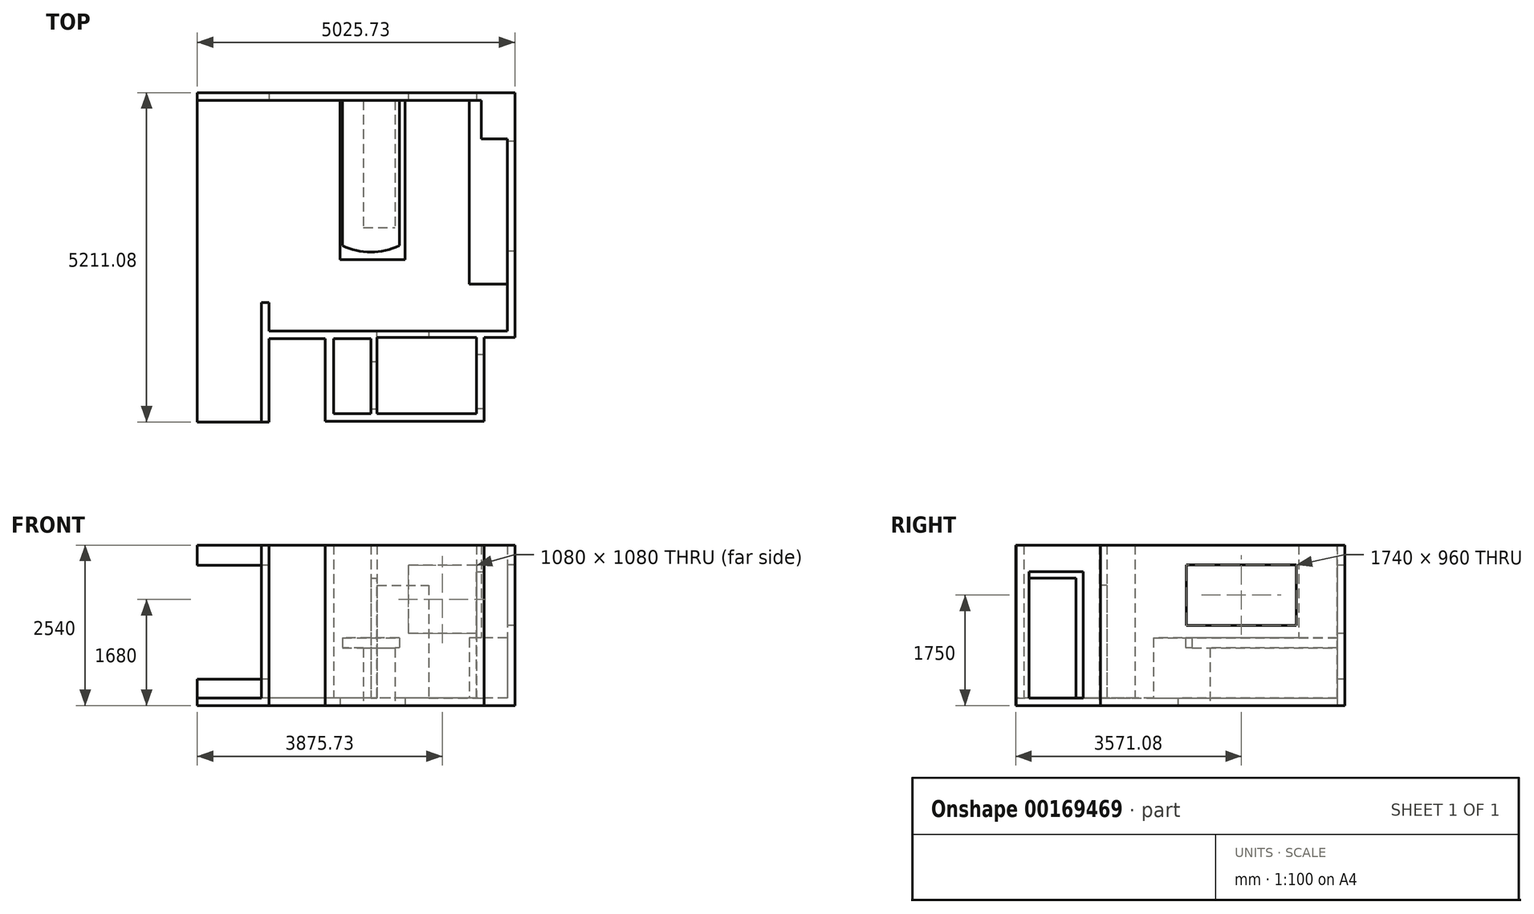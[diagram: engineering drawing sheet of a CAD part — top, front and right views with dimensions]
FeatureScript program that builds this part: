
annotation { "Feature Type Name" : "Feature", "Feature Type Description" : "" }
export const myFeature = defineFeature(function(context is Context, id is Id, definition is map)
    precondition{}
    {
        {
            var Q0;
            Q0=qCreatedBy(makeId("Top.planeOp"),FACE);
            var sketch = newSketch(context, id + "F0", { "sketchPlane" : qUnion([Q0])});
            skLineSegment(sketch, "E0", {"start": v(0, 0) * mm, "end": v(-410, 0) * mm});
            skLineSegment(sketch, "E1", {"start": v(-410, 0) * mm, "end": v(-1710, 0) * mm});
            skLineSegment(sketch, "E2", {"start": v(-1710, 0) * mm, "end": v(-2610, 0) * mm});
            skLineSegment(sketch, "E3", {"start": v(-2610, 0) * mm, "end": v(-3770, 0) * mm});
            skLineSegment(sketch, "E4", {"start": v(0, 0) * mm, "end": v(0, -610) * mm});
            skLineSegment(sketch, "E5", {"start": v(0, -610) * mm, "end": v(0, -2910) * mm});
            skLineSegment(sketch, "E6", {"start": v(0, -2910) * mm, "end": v(0, -3650) * mm});
            skLineSegment(sketch, "E7", {"start": v(0, -3650) * mm, "end": v(-1240, -3650) * mm});
            skLineSegment(sketch, "E8", {"start": v(-1240, -3650) * mm, "end": v(-1240, -3750) * mm});
            skLineSegment(sketch, "E9", {"start": v(-1240, -3750) * mm, "end": v(-490, -3750) * mm});
            skLineSegment(sketch, "E10", {"start": v(-370, -3750) * mm, "end": v(0, -3750) * mm});
            skLineSegment(sketch, "E11", {"start": v(-490, -3750) * mm, "end": v(-490, -4960) * mm});
            skLineSegment(sketch, "E12", {"start": v(-490, -4960) * mm, "end": v(-2060, -4960) * mm});
            skLineSegment(sketch, "E13", {"start": v(-2160, -4960) * mm, "end": v(-2750, -4960) * mm});
            skLineSegment(sketch, "E14", {"start": v(-2060, -4960) * mm, "end": v(-2060, -3650) * mm});
            skLineSegment(sketch, "E15", {"start": v(-2060, -3650) * mm, "end": v(-2670, -3650) * mm});
            skLineSegment(sketch, "E16", {"start": v(-2670, -3650) * mm, "end": v(-3770, -3650) * mm});
            skLineSegment(sketch, "E17", {"start": v(-3770, -3650) * mm, "end": v(-3770, -3200) * mm});
            skLineSegment(sketch, "E18", {"start": v(-3770, -3200) * mm, "end": v(-3890, -3200) * mm});
            skLineSegment(sketch, "E19", {"start": v(-3890, -3200) * mm, "end": v(-3890, -8062.06) * mm});
            skLineSegment(sketch, "E20", {"start": v(-3770, -5080) * mm, "end": v(-3770, -5212) * mm});
            skLineSegment(sketch, "E21", {"start": v(-2750, -5080) * mm, "end": v(-2880, -5080) * mm});
            skLineSegment(sketch, "E22", {"start": v(0, -2910) * mm, "end": v(-600, -2910) * mm});
            skLineSegment(sketch, "E23", {"start": v(-600, -2910) * mm, "end": v(-600, 0) * mm});
            skLineSegment(sketch, "E24", {"start": v(-1710, 0) * mm, "end": v(-1710, -2300) * mm});
            skLineSegment(sketch, "E25", {"start": v(-1710, -2300) * mm, "end": v(-2610, -2300) * mm});
            skLineSegment(sketch, "E26", {"start": v(-2610, -2300) * mm, "end": v(-2610, 0) * mm});
            skLineSegment(sketch, "E27", {"start": v(-2160, 0) * mm, "end": v(-2160, -2400) * mm});
            skArc(sketch, "E28", {"start": v(-2610, -2300) * mm, "mid": v(-2160, -2400) * mm, "end": v(-1710, -2300) * mm});
            skLineSegment(sketch, "E29", {"start": v(-3770, 0) * mm, "end": v(-9401.46, 0) * mm});
            skLineSegment(sketch, "E30", {"start": v(-9401.46, 0) * mm, "end": v(-9401.46, -8062.06) * mm});
            skLineSegment(sketch, "E31", {"start": v(-9401.46, -8062.06) * mm, "end": v(-3890, -8062.06) * mm});
            skLineSegment(sketch, "E32.0", {"start": v(-9521.46, 120) * mm, "end": v(-9521.46, -8050.8) * mm});
            skLineSegment(sketch, "E32.1", {"start": v(-3660, 120) * mm, "end": v(-9521.46, 120) * mm});
            skLineSegment(sketch, "E32.2", {"start": v(-2610, 120) * mm, "end": v(-3660, 120) * mm});
            skLineSegment(sketch, "E32.3", {"start": v(-1710, 120) * mm, "end": v(-2610, 120) * mm});
            skLineSegment(sketch, "E32.4", {"start": v(-410, 120) * mm, "end": v(-1710, 120) * mm});
            skLineSegment(sketch, "E32.5", {"start": v(120, 120) * mm, "end": v(-410, 120) * mm});
            skLineSegment(sketch, "E32.6", {"start": v(120, -3650) * mm, "end": v(120, -3750) * mm});
            skLineSegment(sketch, "E32.7", {"start": v(120, -2910) * mm, "end": v(120, -3650) * mm});
            skLineSegment(sketch, "E32.8", {"start": v(120, -610) * mm, "end": v(120, -2910) * mm});
            skLineSegment(sketch, "E32.9", {"start": v(120, 120) * mm, "end": v(120, -610) * mm});
            skLineSegment(sketch, "E33.0", {"start": v(-2060, -5080) * mm, "end": v(-2750, -5080) * mm});
            skLineSegment(sketch, "E33.1", {"start": v(-370, -5080) * mm, "end": v(-2060, -5080) * mm});
            skLineSegment(sketch, "E33.2", {"start": v(-370, -3750) * mm, "end": v(-370, -5080) * mm});
            skLineSegment(sketch, "E34", {"start": v(-2880, -5080) * mm, "end": v(-2880, -3770) * mm});
            skLineSegment(sketch, "E35", {"start": v(-2880, -3770) * mm, "end": v(-3770, -3770) * mm});
            skLineSegment(sketch, "E36", {"start": v(-2750, -4960) * mm, "end": v(-2750, -3770) * mm});
            skLineSegment(sketch, "E37", {"start": v(-2750, -3770) * mm, "end": v(-2160, -3770) * mm});
            skLineSegment(sketch, "E38", {"start": v(-2160, -3770) * mm, "end": v(-2160, -4960) * mm});
            skLineSegment(sketch, "E39", {"start": v(-9521.46, -8050.8) * mm, "end": v(-9521.46, -8182.06) * mm});
            skLineSegment(sketch, "E40", {"start": v(-9521.46, -8182.06) * mm, "end": v(-3770, -8182.06) * mm});
            skLineSegment(sketch, "E41", {"start": v(-3770, -8182.06) * mm, "end": v(-3770, -5212) * mm});
            skPoint(sketch, "E42.orphan", {"position": v(-2880, -4960) * mm});
            skLineSegment(sketch, "E43", {"start": v(0, -3750) * mm, "end": v(120, -3750) * mm});
            skLineSegment(sketch, "E44", {"start": v(-3770, -5080) * mm, "end": v(-3770, -3770) * mm});
            skSolve(sketch);
        }
        {
            var Q0;
            {var subQ0=sQuery(id+"F0.wireOp",EDGE,"E26");Q0=makeQuery(id+"F0.imprint","IMPRINT",FACE,{"disambiguationData":[TD([[makeQuery(id+"F0.imprint","IMPRINT",EDGE,{"derivedFrom":subQ0}),-1.0]])]});}
            var Q1;
            {var subQ0=sQuery(id+"F0.wireOp",EDGE,"E24");Q1=makeQuery(id+"F0.imprint","IMPRINT",FACE,{"disambiguationData":[TD([[makeQuery(id+"F0.imprint","IMPRINT",EDGE,{"derivedFrom":subQ0}),-1.0]])]});}
            var Q2;
            {var subQ0=sQuery(id+"F0.wireOp",EDGE,"E28");var subQ3=sQuery(id+"F0.wireOp",EDGE,"E27");var subQ5=makeQuery(id+"F0.imprint","INTERSECT",VERTEX,{"derivedFrom":[subQ3,subQ0]});Q2=makeQuery(id+"F0.imprint","IMPRINT",FACE,{"disambiguationData":[TD([[makeQuery(id+"F0.imprint","IMPRINT",EDGE,{"disambiguationData":[TD([[subQ5,1.0]])],"derivedFrom":subQ3}),-1.0]])]});}
            var Q3;
            {var subQ0=sQuery(id+"F0.wireOp",EDGE,"E28");var subQ3=sQuery(id+"F0.wireOp",EDGE,"E27");var subQ5=makeQuery(id+"F0.imprint","INTERSECT",VERTEX,{"derivedFrom":[subQ3,subQ0]});Q3=makeQuery(id+"F0.imprint","IMPRINT",FACE,{"disambiguationData":[TD([[makeQuery(id+"F0.imprint","IMPRINT",EDGE,{"disambiguationData":[TD([[subQ5,1.0]])],"derivedFrom":subQ3}),1.0]])]});}
            var Q4;
            {var subQ2=sQuery(id+"F0.wireOp",EDGE,"E0");Q4=makeQuery(id+"F0.imprint","IMPRINT",FACE,{"disambiguationData":[TD([[makeQuery(id+"F0.imprint","IMPRINT",EDGE,{"derivedFrom":subQ2}),1.0]])]});}
            extrude(context, id + "F1", {"entities" : qUnion([Q0, Q1, Q2, Q3, Q4]), "depth" : 1070 * mm});
        }
        {
            var Q0;
            Q0=makeQuery(id+"F0.imprint","IMPRINT",FACE,{"disambiguationData":[TD([[makeQuery(id+"F0.imprint","IMPRINT",EDGE,{"derivedFrom":sQuery(id+"F0.wireOp",EDGE,"E3")}),1.0]])]});
            var Q1;
            {var subQ0=sQuery(id+"F0.wireOp",EDGE,"E26");Q1=makeQuery(id+"F0.imprint","IMPRINT",FACE,{"disambiguationData":[TD([[makeQuery(id+"F0.imprint","IMPRINT",EDGE,{"derivedFrom":subQ0}),-1.0]])]});}
            var Q2;
            {var subQ0=sQuery(id+"F0.wireOp",EDGE,"E24");Q2=makeQuery(id+"F0.imprint","IMPRINT",FACE,{"disambiguationData":[TD([[makeQuery(id+"F0.imprint","IMPRINT",EDGE,{"derivedFrom":subQ0}),-1.0]])]});}
            var Q3;
            {var subQ0=sQuery(id+"F0.wireOp",EDGE,"E28");var subQ3=sQuery(id+"F0.wireOp",EDGE,"E27");var subQ5=makeQuery(id+"F0.imprint","INTERSECT",VERTEX,{"derivedFrom":[subQ3,subQ0]});Q3=makeQuery(id+"F0.imprint","IMPRINT",FACE,{"disambiguationData":[TD([[makeQuery(id+"F0.imprint","IMPRINT",EDGE,{"disambiguationData":[TD([[subQ5,1.0]])],"derivedFrom":subQ3}),1.0]])]});}
            var Q4;
            {var subQ0=sQuery(id+"F0.wireOp",EDGE,"E28");var subQ3=sQuery(id+"F0.wireOp",EDGE,"E27");var subQ5=makeQuery(id+"F0.imprint","INTERSECT",VERTEX,{"derivedFrom":[subQ3,subQ0]});Q4=makeQuery(id+"F0.imprint","IMPRINT",FACE,{"disambiguationData":[TD([[makeQuery(id+"F0.imprint","IMPRINT",EDGE,{"disambiguationData":[TD([[subQ5,1.0]])],"derivedFrom":subQ3}),-1.0]])]});}
            var Q5;
            {var subQ2=sQuery(id+"F0.wireOp",EDGE,"E0");Q5=makeQuery(id+"F0.imprint","IMPRINT",FACE,{"disambiguationData":[TD([[makeQuery(id+"F0.imprint","IMPRINT",EDGE,{"derivedFrom":subQ2}),1.0]])]});}
            var Q6;
            Q6=makeQuery(id+"F0.imprint","IMPRINT",FACE,{"disambiguationData":[TD([[makeQuery(id+"F0.imprint","IMPRINT",EDGE,{"derivedFrom":sQuery(id+"F0.wireOp",EDGE,"iXBZxJ0I-YXaI-NLH3-BIux-PB3kZKphdtHV")}),-1.0]])]});
            var Q7;
            Q7=makeQuery(id+"F0.imprint","IMPRINT",FACE,{"disambiguationData":[TD([[makeQuery(id+"F0.imprint","IMPRINT",EDGE,{"derivedFrom":sQuery(id+"F0.wireOp",EDGE,"E13")}),-1.0]])]});
            extrude(context, id + "F2", {"entities" : qUnion([Q0, Q1, Q2, Q3, Q4, Q5, Q6, Q7]), "depth" : 120 * mm});
        }
        {
            var Q0;
            {var subQ1=sQuery(id+"F0.wireOp",EDGE,"E0");Q0=makeQuery(id+"F0.imprint","IMPRINT",FACE,{"disambiguationData":[TD([[makeQuery(id+"F0.imprint","IMPRINT",EDGE,{"derivedFrom":subQ1}),-1.0]])]});}
            extrude(context, id + "F3", {"entities" : qUnion([Q0]), "operationType" : NewBodyOperationType.ADD, "depth" : 2540 * mm});
        }
        {
            var Q0;
            Q0=makeQuery(id+"F3.opExtrude","SWEPT_FACE",FACE,{"disambiguationData":[OSD([sQuery(id+"F0.wireOp",EDGE,"E4"),sQuery(id+"F0.wireOp",EDGE,"E5"),sQuery(id+"F0.wireOp",EDGE,"E6")])]});
            var sketch = newSketch(context, id + "F4", { "sketchPlane" : qUnion([Q0])});
            skLineSegment(sketch, "E45.bottom", {"start": v(650, 2230) * mm, "end": v(2390, 2230) * mm});
            skLineSegment(sketch, "E45.top", {"start": v(650, 1270) * mm, "end": v(2390, 1270) * mm});
            skLineSegment(sketch, "E45.left", {"start": v(650, 2230) * mm, "end": v(650, 1270) * mm});
            skLineSegment(sketch, "E45.right", {"start": v(2390, 2230) * mm, "end": v(2390, 1270) * mm});
            skSolve(sketch);
        }
        {
            var Q0;
            Q0 = qSketchRegion(id + "F4", true);
            extrude(context, id + "F5", {"entities" : qUnion([Q0]), "operationType" : NewBodyOperationType.REMOVE, "endBound" : BoundingType.UP_TO_NEXT, "oppositeDirection" : true, "depth" : 25 * mm});
        }
        {
            var Q0;
            Q0=makeQuery(id+"F3.opExtrude","SWEPT_FACE",FACE,{"disambiguationData":[OSD([sQuery(id+"F0.wireOp",EDGE,"E0"),sQuery(id+"F0.wireOp",EDGE,"E1"),sQuery(id+"F0.wireOp",EDGE,"E2"),sQuery(id+"F0.wireOp",EDGE,"E3"),sQuery(id+"F0.wireOp",EDGE,"E29")])]});
            var sketch = newSketch(context, id + "F6", { "sketchPlane" : qUnion([Q0])});
            skLineSegment(sketch, "E46.bottom", {"start": v(-490, 2220) * mm, "end": v(-1570, 2220) * mm});
            skLineSegment(sketch, "E46.top", {"start": v(-490, 1140) * mm, "end": v(-1570, 1140) * mm});
            skLineSegment(sketch, "E46.left", {"start": v(-490, 2220) * mm, "end": v(-490, 1140) * mm});
            skLineSegment(sketch, "E46.right", {"start": v(-1570, 2220) * mm, "end": v(-1570, 1140) * mm});
            skSolve(sketch);
        }
        {
            var Q0;
            Q0 = qSketchRegion(id + "F6", true);
            extrude(context, id + "F7", {"entities" : qUnion([Q0]), "operationType" : NewBodyOperationType.REMOVE, "endBound" : BoundingType.UP_TO_NEXT, "oppositeDirection" : true, "depth" : 25 * mm});
        }
        {
            var Q0;
            Q0=makeQuery(id+"F1.opExtrude","CAP_FACE",FACE,{"disambiguationData":[OSD([sQuery(id+"F0.wireOp",EDGE,"E0"),sQuery(id+"F0.wireOp",EDGE,"E1"),sQuery(id+"F0.wireOp",EDGE,"E4"),sQuery(id+"F0.wireOp",EDGE,"E5"),sQuery(id+"F0.wireOp",EDGE,"E22"),sQuery(id+"F0.wireOp",EDGE,"E23")])],"isStart":false});
            var sketch = newSketch(context, id + "F8", { "sketchPlane" : qUnion([Q0])});
            skLineSegment(sketch, "E47.bottom", {"start": v(0, 0) * mm, "end": v(-410, 0) * mm});
            skLineSegment(sketch, "E47.top", {"start": v(0, -610) * mm, "end": v(-410, -610) * mm});
            skLineSegment(sketch, "E47.left", {"start": v(0, 0) * mm, "end": v(0, -610) * mm});
            skLineSegment(sketch, "E47.right", {"start": v(-410, 0) * mm, "end": v(-410, -610) * mm});
            skSolve(sketch);
        }
        {
            var Q0;
            Q0 = qSketchRegion(id + "F8", true);
            var Q1;
            Q1=makeQuery(id+"F3.opExtrude","CAP_FACE",FACE,{"disambiguationData":[OSD([sQuery(id+"F0.wireOp",EDGE,"E0"),sQuery(id+"F0.wireOp",EDGE,"E1"),sQuery(id+"F0.wireOp",EDGE,"E2"),sQuery(id+"F0.wireOp",EDGE,"E3"),sQuery(id+"F0.wireOp",EDGE,"E4"),sQuery(id+"F0.wireOp",EDGE,"E5"),sQuery(id+"F0.wireOp",EDGE,"E6"),sQuery(id+"F0.wireOp",EDGE,"E7"),sQuery(id+"F0.wireOp",EDGE,"E8"),sQuery(id+"F0.wireOp",EDGE,"E9"),sQuery(id+"F0.wireOp",EDGE,"E10"),sQuery(id+"F0.wireOp",EDGE,"E11"),sQuery(id+"F0.wireOp",EDGE,"E12"),sQuery(id+"F0.wireOp",EDGE,"E13"),sQuery(id+"F0.wireOp",EDGE,"E14"),sQuery(id+"F0.wireOp",EDGE,"E15"),sQuery(id+"F0.wireOp",EDGE,"E16"),sQuery(id+"F0.wireOp",EDGE,"E17"),sQuery(id+"F0.wireOp",EDGE,"E18"),sQuery(id+"F0.wireOp",EDGE,"E19"),sQuery(id+"F0.wireOp",EDGE,"E20"),sQuery(id+"F0.wireOp",EDGE,"E21"),sQuery(id+"F0.wireOp",EDGE,"E29"),sQuery(id+"F0.wireOp",EDGE,"E30"),sQuery(id+"F0.wireOp",EDGE,"E31"),sQuery(id+"F0.wireOp",EDGE,"E32.0"),sQuery(id+"F0.wireOp",EDGE,"E32.1"),sQuery(id+"F0.wireOp",EDGE,"E32.2"),sQuery(id+"F0.wireOp",EDGE,"E32.3"),sQuery(id+"F0.wireOp",EDGE,"E32.4"),sQuery(id+"F0.wireOp",EDGE,"E32.5"),sQuery(id+"F0.wireOp",EDGE,"E32.6"),sQuery(id+"F0.wireOp",EDGE,"E32.7"),sQuery(id+"F0.wireOp",EDGE,"E32.8"),sQuery(id+"F0.wireOp",EDGE,"E32.9"),sQuery(id+"F0.wireOp",EDGE,"E33.0"),sQuery(id+"F0.wireOp",EDGE,"E33.1"),sQuery(id+"F0.wireOp",EDGE,"E33.2"),sQuery(id+"F0.wireOp",EDGE,"E34"),sQuery(id+"F0.wireOp",EDGE,"E35"),sQuery(id+"F0.wireOp",EDGE,"E36"),sQuery(id+"F0.wireOp",EDGE,"E37"),sQuery(id+"F0.wireOp",EDGE,"E38"),sQuery(id+"F0.wireOp",EDGE,"E39"),sQuery(id+"F0.wireOp",EDGE,"E40"),sQuery(id+"F0.wireOp",EDGE,"E41"),sQuery(id+"F0.wireOp",EDGE,"iXBZxJ0I-YXaI-NLH3-BIux-PB3kZKphdtHV"),sQuery(id+"F0.wireOp",EDGE,"v6Kazt3i-zFhM-lRUx-sptf-w9UfosPWx9Ew"),sQuery(id+"F0.wireOp",EDGE,"KXPRrlc0-wEXm-2mnN-JFA4-RJdvIjk6WKE2"),sQuery(id+"F0.wireOp",EDGE,"E43"),sQuery(id+"F0.wireOp",EDGE,"E44"),sQuery(id+"F0.wireOp",EDGE,"do1nGqsm-fpm6-EWKF-r1zN-ITFsnXuoGL9v")])],"isStart":false});
            extrude(context, id + "F9", {"entities" : qUnion([Q0]), "operationType" : NewBodyOperationType.ADD, "endBound" : BoundingType.UP_TO_SURFACE, "endBoundEntityFace" : qUnion([Q1]), "depth" : 1410 * mm});
        }
        {
            var Q0;
            Q0=makeQuery(id+"F3.opExtrude","SWEPT_FACE",FACE,{"disambiguationData":[OSD([sQuery(id+"F0.wireOp",EDGE,"E0"),sQuery(id+"F0.wireOp",EDGE,"E1"),sQuery(id+"F0.wireOp",EDGE,"E2"),sQuery(id+"F0.wireOp",EDGE,"E3"),sQuery(id+"F0.wireOp",EDGE,"E29")])]});
            var sketch = newSketch(context, id + "F10", { "sketchPlane" : qUnion([Q0])});
            skLineSegment(sketch, "E48.bottom", {"start": v(-3770, 420) * mm, "end": v(-9315.52, 420) * mm});
            skLineSegment(sketch, "E48.top", {"start": v(-3770, 2220) * mm, "end": v(-9315.52, 2220) * mm});
            skLineSegment(sketch, "E48.left", {"start": v(-3770, 420) * mm, "end": v(-3770, 2220) * mm});
            skLineSegment(sketch, "E48.right", {"start": v(-9315.52, 420) * mm, "end": v(-9315.52, 2220) * mm});
            skSolve(sketch);
        }
        {
            var Q0;
            Q0 = qSketchRegion(id + "F10", true);
            extrude(context, id + "F11", {"entities" : qUnion([Q0]), "operationType" : NewBodyOperationType.REMOVE, "endBound" : BoundingType.UP_TO_NEXT, "oppositeDirection" : true, "depth" : 25 * mm});
        }
        {
            var Q0;
            {var subQ0=sQuery(id+"F0.wireOp",EDGE,"E26");Q0=makeQuery(id+"F0.imprint","IMPRINT",FACE,{"disambiguationData":[TD([[makeQuery(id+"F0.imprint","IMPRINT",EDGE,{"derivedFrom":subQ0}),-1.0]])]});}
            var sketch = newSketch(context, id + "F12", { "sketchPlane" : qUnion([Q0])});
            skLineSegment(sketch, "E49.bottom", {"start": v(-2275.66, 0) * mm, "end": v(-1778.73, 0) * mm});
            skLineSegment(sketch, "E49.top", {"start": v(-2275.66, -2013.54) * mm, "end": v(-1778.73, -2013.54) * mm});
            skLineSegment(sketch, "E49.left", {"start": v(-2275.66, 0) * mm, "end": v(-2275.66, -2013.54) * mm});
            skLineSegment(sketch, "E49.right", {"start": v(-1778.73, 0) * mm, "end": v(-1778.73, -2013.54) * mm});
            skLineSegment(sketch, "E50", {"start": v(-2275.66, 0) * mm, "end": v(-2647.7, 0) * mm});
            skLineSegment(sketch, "E51", {"start": v(-2647.7, 0) * mm, "end": v(-2647.7, -2522.37) * mm});
            skLineSegment(sketch, "E52", {"start": v(-2647.7, -2522.37) * mm, "end": v(-1617.56, -2522.37) * mm});
            skLineSegment(sketch, "E53", {"start": v(-1617.56, -2522.37) * mm, "end": v(-1617.56, 0) * mm});
            skLineSegment(sketch, "E54", {"start": v(-1617.56, 0) * mm, "end": v(-1778.73, 0) * mm});
            skSolve(sketch);
        }
        {
            var Q0;
            {var subQ1=sQuery(id+"F12.wireOp",EDGE,"E49.right");Q0=makeQuery(id+"F12.imprint","IMPRINT",FACE,{"disambiguationData":[TD([[makeQuery(id+"F12.imprint","IMPRINT",EDGE,{"derivedFrom":subQ1}),1.0]])]});}
            var Q1;
            {var subQ3=sQuery(id+"F12.wireOp",EDGE,"E49.left");Q1=makeQuery(id+"F12.imprint","IMPRINT",FACE,{"disambiguationData":[TD([[makeQuery(id+"F12.imprint","IMPRINT",EDGE,{"derivedFrom":subQ3}),-1.0]])]});}
            extrude(context, id + "F13", {"entities" : qUnion([Q0, Q1]), "operationType" : NewBodyOperationType.REMOVE, "depth" : 912 * mm});
        }
        {
            var Q0;
            Q0=makeQuery(id+"F3.opExtrude","SWEPT_FACE",FACE,{"disambiguationData":[OSD([sQuery(id+"F0.wireOp",EDGE,"E8")])]});
            var sketch = newSketch(context, id + "F14", { "sketchPlane" : qUnion([Q0])});
            skLineSegment(sketch, "E55.bottom", {"start": v(3650, 2540) * mm, "end": v(3750, 2540) * mm});
            skLineSegment(sketch, "E55.top", {"start": v(3650, 1903.57) * mm, "end": v(3750, 1903.57) * mm});
            skLineSegment(sketch, "E55.left", {"start": v(3650, 2540) * mm, "end": v(3650, 1903.57) * mm});
            skLineSegment(sketch, "E55.right", {"start": v(3750, 2540) * mm, "end": v(3750, 1903.57) * mm});
            skSolve(sketch);
        }
        {
            var Q0;
            Q0 = qSketchRegion(id + "F14", true);
            extrude(context, id + "F15", {"entities" : qUnion([Q0]), "operationType" : NewBodyOperationType.ADD, "endBound" : BoundingType.UP_TO_NEXT, "depth" : 25 * mm});
        }
        {
            var Q0;
            {var subQ0=sQuery(id+"F0.wireOp",EDGE,"do1nGqsm-fpm6-EWKF-r1zN-ITFsnXuoGL9v");var subQ1=sQuery(id+"F0.wireOp",EDGE,"E44");var subQ2=sQuery(id+"F0.wireOp",EDGE,"E43");var subQ3=sQuery(id+"F0.wireOp",EDGE,"KXPRrlc0-wEXm-2mnN-JFA4-RJdvIjk6WKE2");var subQ4=sQuery(id+"F0.wireOp",EDGE,"v6Kazt3i-zFhM-lRUx-sptf-w9UfosPWx9Ew");var subQ5=sQuery(id+"F0.wireOp",EDGE,"iXBZxJ0I-YXaI-NLH3-BIux-PB3kZKphdtHV");var subQ6=sQuery(id+"F0.wireOp",EDGE,"E41");var subQ7=sQuery(id+"F0.wireOp",EDGE,"E40");var subQ8=sQuery(id+"F0.wireOp",EDGE,"E39");var subQ9=sQuery(id+"F0.wireOp",EDGE,"E38");var subQ10=sQuery(id+"F0.wireOp",EDGE,"E37");var subQ11=sQuery(id+"F0.wireOp",EDGE,"E36");var subQ12=sQuery(id+"F0.wireOp",EDGE,"E35");var subQ13=sQuery(id+"F0.wireOp",EDGE,"E34");var subQ14=sQuery(id+"F0.wireOp",EDGE,"E33.2");var subQ15=sQuery(id+"F0.wireOp",EDGE,"E33.1");var subQ16=sQuery(id+"F0.wireOp",EDGE,"E33.0");var subQ17=sQuery(id+"F0.wireOp",EDGE,"E32.9");var subQ18=sQuery(id+"F0.wireOp",EDGE,"E32.8");var subQ19=sQuery(id+"F0.wireOp",EDGE,"E32.7");var subQ20=sQuery(id+"F0.wireOp",EDGE,"E32.6");var subQ21=sQuery(id+"F0.wireOp",EDGE,"E32.5");var subQ22=sQuery(id+"F0.wireOp",EDGE,"E32.4");var subQ23=sQuery(id+"F0.wireOp",EDGE,"E32.3");var subQ24=sQuery(id+"F0.wireOp",EDGE,"E32.2");var subQ25=sQuery(id+"F0.wireOp",EDGE,"E32.1");var subQ26=sQuery(id+"F0.wireOp",EDGE,"E32.0");var subQ27=sQuery(id+"F0.wireOp",EDGE,"E31");var subQ28=sQuery(id+"F0.wireOp",EDGE,"E30");var subQ29=sQuery(id+"F0.wireOp",EDGE,"E29");var subQ30=sQuery(id+"F0.wireOp",EDGE,"E21");var subQ31=sQuery(id+"F0.wireOp",EDGE,"E20");var subQ32=sQuery(id+"F0.wireOp",EDGE,"E19");var subQ33=sQuery(id+"F0.wireOp",EDGE,"E18");var subQ34=sQuery(id+"F0.wireOp",EDGE,"E17");var subQ35=sQuery(id+"F0.wireOp",EDGE,"E16");var subQ36=sQuery(id+"F0.wireOp",EDGE,"E15");var subQ37=sQuery(id+"F0.wireOp",EDGE,"E14");var subQ38=sQuery(id+"F0.wireOp",EDGE,"E13");var subQ39=sQuery(id+"F0.wireOp",EDGE,"E12");var subQ40=sQuery(id+"F0.wireOp",EDGE,"E11");var subQ41=sQuery(id+"F0.wireOp",EDGE,"E10");var subQ42=sQuery(id+"F0.wireOp",EDGE,"E9");var subQ43=sQuery(id+"F0.wireOp",EDGE,"E8");var subQ44=sQuery(id+"F0.wireOp",EDGE,"E7");var subQ45=sQuery(id+"F0.wireOp",EDGE,"E6");var subQ46=sQuery(id+"F0.wireOp",EDGE,"E5");var subQ47=sQuery(id+"F0.wireOp",EDGE,"E4");var subQ48=sQuery(id+"F0.wireOp",EDGE,"E3");var subQ49=sQuery(id+"F0.wireOp",EDGE,"E2");var subQ50=sQuery(id+"F0.wireOp",EDGE,"E1");var subQ51=sQuery(id+"F0.wireOp",EDGE,"E0");Q0=makeQuery(id+"F15.boolean.opBoolean","MERGE",FACE,{"derivedFrom":[makeQuery(id+"F9.boolean.opBoolean","MERGE",FACE,{"derivedFrom":[makeQuery(id+"F3.opExtrude","CAP_FACE",FACE,{"disambiguationData":[OSD([subQ51,subQ50,subQ49,subQ48,subQ47,subQ46,subQ45,subQ44,subQ43,subQ42,subQ41,subQ40,subQ39,subQ38,subQ37,subQ36,subQ35,subQ34,subQ33,subQ32,subQ31,subQ30,subQ29,subQ28,subQ27,subQ26,subQ25,subQ24,subQ23,subQ22,subQ21,subQ20,subQ19,subQ18,subQ17,subQ16,subQ15,subQ14,subQ13,subQ12,subQ11,subQ10,subQ9,subQ8,subQ7,subQ6,subQ5,subQ4,subQ3,subQ2,subQ1,subQ0])],"isStart":false}),makeQuery(id+"F9.opExtrude","CAP_FACE",FACE,{"disambiguationData":[OSD([subQ51,subQ50,subQ49,subQ48,subQ47,subQ46,subQ45,subQ44,subQ43,subQ42,subQ41,subQ40,subQ39,subQ38,subQ37,subQ36,subQ35,subQ34,subQ33,subQ32,subQ31,subQ30,subQ29,subQ28,subQ27,subQ26,subQ25,subQ24,subQ23,subQ22,subQ21,subQ20,subQ19,subQ18,subQ17,subQ16,subQ15,subQ14,subQ13,subQ12,subQ11,subQ10,subQ9,subQ8,subQ7,subQ6,subQ5,subQ4,subQ3,subQ2,subQ1,subQ0])],"isStart":false})]}),makeQuery(id+"F15.opExtrude","SWEPT_FACE",FACE,{"disambiguationData":[OSD([sQuery(id+"F14.wireOp",EDGE,"E55.bottom")])]})]});}
            var sketch = newSketch(context, id + "F16", { "sketchPlane" : qUnion([Q0])});
            skPoint(sketch, "E56.oppositeSnap0", {"position": v(-4905.73, 0) * mm});
            skLineSegment(sketch, "E56.bottom", {"start": v(-9521.46, -8182.06) * mm, "end": v(-4905.73, -8182.06) * mm});
            skLineSegment(sketch, "E56.top", {"start": v(-9521.46, 120) * mm, "end": v(-4905.73, 120) * mm});
            skLineSegment(sketch, "E56.left", {"start": v(-9521.46, -8182.06) * mm, "end": v(-9521.46, 120) * mm});
            skLineSegment(sketch, "E56.right", {"start": v(-4905.73, -8182.06) * mm, "end": v(-4905.73, 120) * mm});
            skLineSegment(sketch, "E57.bottom", {"start": v(-3770, -8182.06) * mm, "end": v(-4905.73, -8182.06) * mm});
            skLineSegment(sketch, "E57.top", {"start": v(-3770, -5091.08) * mm, "end": v(-4905.73, -5091.08) * mm});
            skLineSegment(sketch, "E57.left", {"start": v(-3770, -8182.06) * mm, "end": v(-3770, -5091.08) * mm});
            skLineSegment(sketch, "E57.right", {"start": v(-4905.73, -8182.06) * mm, "end": v(-4905.73, -5091.08) * mm});
            skSolve(sketch);
        }
        {
            var Q0;
            Q0 = qSketchRegion(id + "F16", true);
            extrude(context, id + "F17", {"entities" : qUnion([Q0]), "operationType" : NewBodyOperationType.REMOVE, "oppositeDirection" : true, "depth" : 3240 * mm});
        }
        {
            var Q0;
            Q0=makeQuery(id+"F3.opExtrude","SWEPT_FACE",FACE,{"disambiguationData":[OSD([sQuery(id+"F0.wireOp",EDGE,"E33.2")])]});
            var sketch = newSketch(context, id + "F18", { "sketchPlane" : qUnion([Q0])});
            skLineSegment(sketch, "E58.bottom", {"start": v(-4020, 2120) * mm, "end": v(-4880, 2120) * mm});
            skLineSegment(sketch, "E58.top", {"start": v(-4020, 120) * mm, "end": v(-4880, 120) * mm});
            skLineSegment(sketch, "E58.left", {"start": v(-4020, 2120) * mm, "end": v(-4020, 120) * mm});
            skLineSegment(sketch, "E58.right", {"start": v(-4880, 2120) * mm, "end": v(-4880, 120) * mm});
            skSolve(sketch);
        }
        {
            var Q0;
            Q0 = qSketchRegion(id + "F18", true);
            extrude(context, id + "F19", {"entities" : qUnion([Q0]), "operationType" : NewBodyOperationType.REMOVE, "endBound" : BoundingType.UP_TO_NEXT, "oppositeDirection" : true, "depth" : 25 * mm});
        }
        {
            var Q0;
            Q0=makeQuery(id+"F3.opExtrude","SWEPT_FACE",FACE,{"disambiguationData":[OSD([sQuery(id+"F0.wireOp",EDGE,"E14")])]});
            var sketch = newSketch(context, id + "F20", { "sketchPlane" : qUnion([Q0])});
            skLineSegment(sketch, "E59.bottom", {"start": v(-4883.6, 120) * mm, "end": v(-4133.6, 120) * mm});
            skLineSegment(sketch, "E59.top", {"start": v(-4883.6, 2020) * mm, "end": v(-4133.6, 2020) * mm});
            skLineSegment(sketch, "E59.left", {"start": v(-4883.6, 120) * mm, "end": v(-4883.6, 2020) * mm});
            skLineSegment(sketch, "E59.right", {"start": v(-4133.6, 120) * mm, "end": v(-4133.6, 2020) * mm});
            skSolve(sketch);
        }
        {
            var Q0;
            Q0 = qSketchRegion(id + "F20", true);
            extrude(context, id + "F21", {"entities" : qUnion([Q0]), "operationType" : NewBodyOperationType.REMOVE, "endBound" : BoundingType.UP_TO_NEXT, "oppositeDirection" : true, "depth" : 25 * mm});
        }
    });
